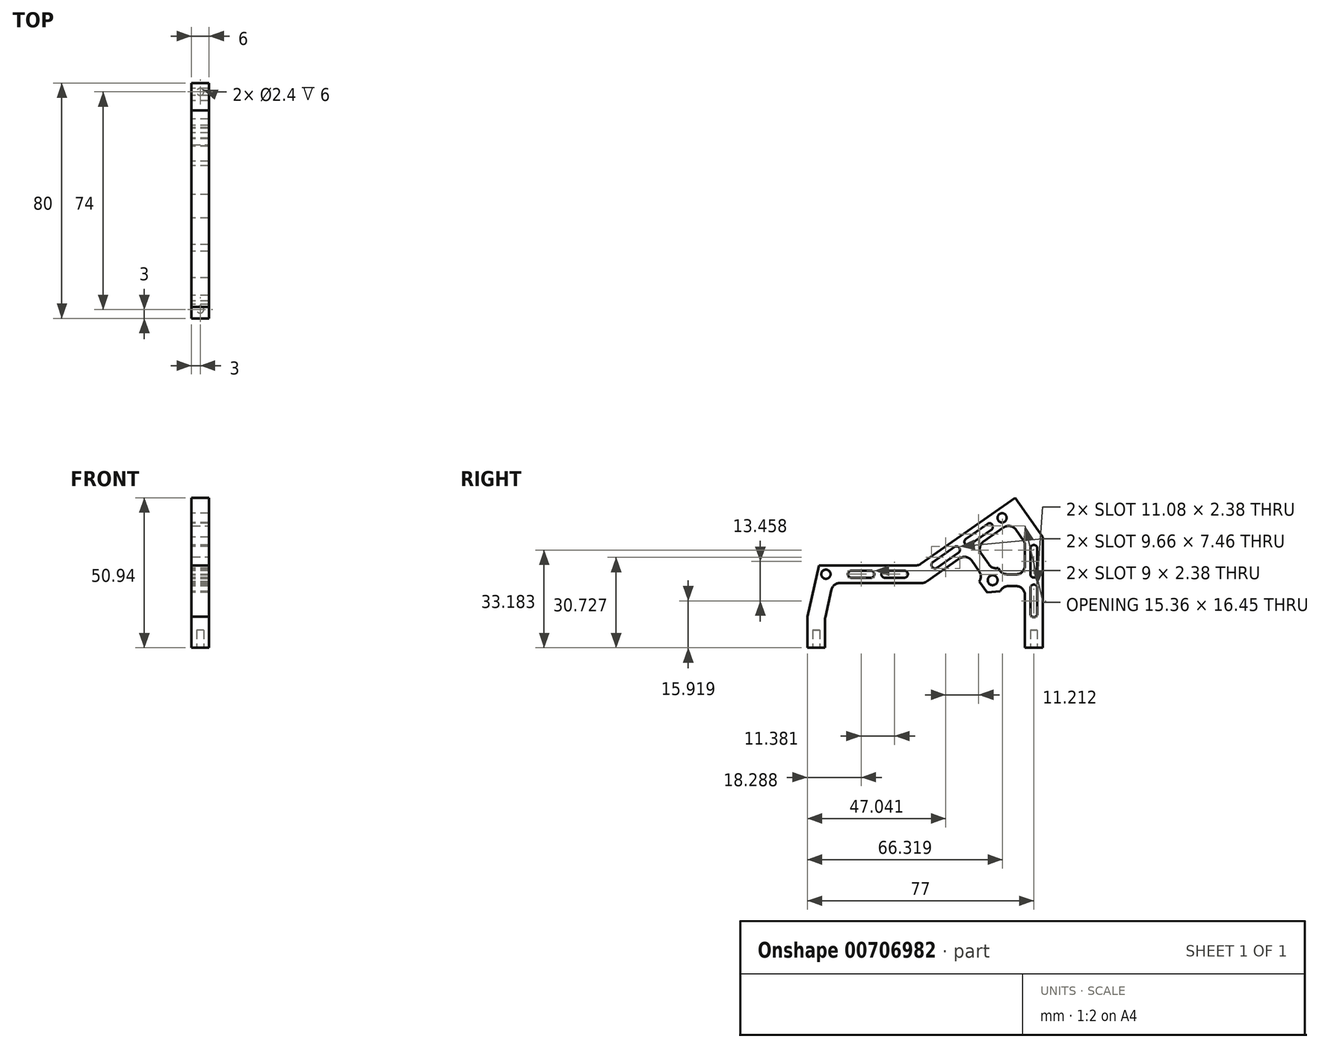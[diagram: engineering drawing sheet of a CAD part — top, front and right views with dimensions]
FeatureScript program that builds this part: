
annotation { "Feature Type Name" : "Feature", "Feature Type Description" : "" }
export const myFeature = defineFeature(function(context is Context, id is Id, definition is map)
    precondition{}
    {
        {
            var Q0;
            Q0=qCreatedBy(makeId("Top.planeOp"),FACE);
            var sketch = newSketch(context, id + "F0", { "sketchPlane" : qUnion([Q0])});
            skLineSegment(sketch, "E0", {"start": v(14, 40) * mm, "end": v(0, 40) * mm, "construction": true});
            skLineSegment(sketch, "E1", {"start": v(0, 40) * mm, "end": v(0, 0) * mm, "construction": true});
            skLineSegment(sketch, "E2", {"start": v(14, 40) * mm, "end": v(20, 40) * mm});
            skLineSegment(sketch, "E3", {"start": v(20, 40) * mm, "end": v(20, 0) * mm});
            skLineSegment(sketch, "E4", {"start": v(14, 40) * mm, "end": v(14, 0) * mm});
            skLineSegment(sketch, "E5.MirrorCS", {"start": v(14, -40) * mm, "end": v(20, -40) * mm});
            skLineSegment(sketch, "E6.MirrorCS", {"start": v(14, -40) * mm, "end": v(14, 0) * mm});
            skLineSegment(sketch, "E7.MirrorCS", {"start": v(20, -40) * mm, "end": v(20, 0) * mm});
            skLineSegment(sketch, "E8.MirrorCS", {"start": v(14, -40) * mm, "end": v(0, -40) * mm, "construction": true});
            skLineSegment(sketch, "E9.MirrorCS", {"start": v(0, -40) * mm, "end": v(0, 0) * mm, "construction": true});
            skLineSegment(sketch, "E10", {"start": v(14, 0) * mm, "end": v(29.88, 0) * mm, "construction": true});
            skLineSegment(sketch, "E11", {"start": v(20, 40) * mm, "end": v(20, 34) * mm, "construction": true});
            skPoint(sketch, "E12.centerSnap0", {"position": v(20, 37) * mm});
            skPoint(sketch, "E12.centerSnap1", {"position": v(17, 40) * mm});
            skSolve(sketch);
        }
        {
            var Q0;
            Q0=makeQuery(id+"F0.imprint","IMPRINT",FACE,{"disambiguationData":[TD([[makeQuery(id+"F0.imprint","IMPRINT",EDGE,{"derivedFrom":sQuery(id+"F0.wireOp",EDGE,"E2")}),-1.0]])]});
            extrude(context, id + "F1", {"entities" : qUnion([Q0]), "depth" : 70 * mm, "offsetDistance" : 25 * mm});
        }
        {
            var Q0;
            Q0=makeQuery(id+"F1.opExtrude","SWEPT_FACE",FACE,{"disambiguationData":[OSD([sQuery(id+"F0.wireOp",EDGE,"E4"),sQuery(id+"F0.wireOp",EDGE,"E6.MirrorCS")])]});
            var sketch = newSketch(context, id + "F2", { "sketchPlane" : qUnion([Q0])});
            skLineSegment(sketch, "E13", {"start": v(0, 0) * mm, "end": v(0, 28) * mm, "construction": true});
            skPoint(sketch, "E13.endSnap0", {"position": v(0, 0) * mm});
            skLineSegment(sketch, "E14", {"start": v(-20.33, 28) * mm, "end": v(19.67, 28) * mm, "construction": true});
            skLineSegment(sketch, "E15", {"start": v(2.08, 28) * mm, "end": v(-30.68, 50.94) * mm});
            skLineSegment(sketch, "E16", {"start": v(40, 10.6) * mm, "end": v(36.08, 28) * mm});
            skLineSegment(sketch, "E17", {"start": v(36.08, 28) * mm, "end": v(2.08, 28) * mm});
            skLineSegment(sketch, "E18", {"start": v(-30.68, 50.94) * mm, "end": v(-40, 37.64) * mm});
            skLineSegment(sketch, "E19", {"start": v(-40, 37.64) * mm, "end": v(-40, 0) * mm});
            skLineSegment(sketch, "E20", {"start": v(31.28, 22) * mm, "end": v(0.2, 22) * mm});
            skLineSegment(sketch, "E21", {"start": v(0.2, 22) * mm, "end": v(-14.18, 32.07) * mm});
            skLineSegment(sketch, "E22", {"start": v(-29.2, 42.59) * mm, "end": v(-34, 35.74) * mm});
            skLineSegment(sketch, "E23", {"start": v(-34, 35.74) * mm, "end": v(-34, 24.96) * mm});
            skLineSegment(sketch, "E24", {"start": v(-14.18, 32.07) * mm, "end": v(-21.96, 20.96) * mm});
            skLineSegment(sketch, "E25", {"start": v(-21.96, 20.96) * mm, "end": v(-34, 20.96) * mm});
            skLineSegment(sketch, "E26", {"start": v(-17.46, 34.36) * mm, "end": v(-24.04, 24.96) * mm});
            skLineSegment(sketch, "E27", {"start": v(-24.04, 24.96) * mm, "end": v(-34, 24.96) * mm});
            skLineSegment(sketch, "E28", {"start": v(-24.04, 24.96) * mm, "end": v(-21.96, 20.96) * mm, "construction": true});
            skCircle(sketch, "E29", {"center": v(-23, 22.96) * mm, "radius": 1.69 * mm});
            skLineSegment(sketch, "E30.trimOffspring", {"start": v(-17.46, 34.36) * mm, "end": v(-29.2, 42.59) * mm});
            skLineSegment(sketch, "E31.trimOffspring", {"start": v(-34, 20.96) * mm, "end": v(-34, 0) * mm});
            skLineSegment(sketch, "E32", {"start": v(-24.5, 46.6) * mm, "end": v(-26.21, 44.15) * mm, "construction": true});
            skCircle(sketch, "E33", {"center": v(-26.21, 44.15) * mm, "radius": 1.57 * mm});
            skLineSegment(sketch, "E34", {"start": v(36.08, 28) * mm, "end": v(31.28, 22) * mm, "construction": true});
            skCircle(sketch, "E35", {"center": v(33.68, 25) * mm, "radius": 1.57 * mm});
            skCircle(sketch, "E36.cCircle", {"center": v(-23, 22.96) * mm, "radius": 3.92 * mm, "construction": true});
            skLineSegment(sketch, "E36.0", {"start": v(-27.51, 23.35) * mm, "end": v(-24.92, 27.06) * mm});
            skLineSegment(sketch, "E36.1", {"start": v(-24.92, 27.06) * mm, "end": v(-20.4, 26.67) * mm});
            skLineSegment(sketch, "E36.2", {"start": v(-20.4, 26.67) * mm, "end": v(-18.5, 22.56) * mm});
            skLineSegment(sketch, "E36.3", {"start": v(-18.5, 22.56) * mm, "end": v(-21.09, 18.85) * mm});
            skLineSegment(sketch, "E36.4", {"start": v(-21.09, 18.85) * mm, "end": v(-25.6, 19.25) * mm});
            skLineSegment(sketch, "E36.5", {"start": v(-25.6, 19.25) * mm, "end": v(-27.51, 23.35) * mm});
            skPoint(sketch, "E36.0.midPoint", {"position": v(-26.21, 25.2) * mm});
            skLineSegment(sketch, "E37", {"start": v(-30.68, 50.94) * mm, "end": v(-30.68, 0) * mm, "construction": true});
            skLineSegment(sketch, "E38", {"start": v(-49.75, 0) * mm, "end": v(34, 0) * mm, "construction": true});
            skLineSegment(sketch, "E39", {"start": v(40, 10.6) * mm, "end": v(40, 0) * mm});
            skLineSegment(sketch, "E40", {"start": v(40, 0) * mm, "end": v(36.1, 0) * mm});
            skLineSegment(sketch, "E41", {"start": v(34, 9.92) * mm, "end": v(34, 0) * mm});
            skLineSegment(sketch, "E42.trimOffspring", {"start": v(42.25, 0) * mm, "end": v(49.74, 0) * mm, "construction": true});
            skLineSegment(sketch, "E43", {"start": v(40, 0) * mm, "end": v(34, 0) * mm});
            skLineSegment(sketch, "E44", {"start": v(31.28, 22) * mm, "end": v(34, 9.92) * mm});
            skLineSegment(sketch, "E45", {"start": v(0.2, 22) * mm, "end": v(31.28, 22) * mm});
            skLineSegment(sketch, "E46", {"start": v(40, 0) * mm, "end": v(40, 10.6) * mm});
            skLineSegment(sketch, "E47", {"start": v(7.02, 26.2) * mm, "end": v(13.64, 26.2) * mm});
            skLineSegment(sketch, "E48", {"start": v(2.08, 28) * mm, "end": v(2.08, 22) * mm, "construction": true});
            skLineSegment(sketch, "E49", {"start": v(7.02, 23.8) * mm, "end": v(7.02, 26.2) * mm, "construction": true});
            skLineSegment(sketch, "E50", {"start": v(25.02, 23.8) * mm, "end": v(25.02, 26.2) * mm, "construction": true});
            skCircle(sketch, "E51", {"center": v(7.02, 25) * mm, "radius": 1.2 * mm});
            skCircle(sketch, "E52", {"center": v(25.02, 25) * mm, "radius": 1.2 * mm});
            skLineSegment(sketch, "E53", {"start": v(-35.8, 33.72) * mm, "end": v(-35.8, 25.03) * mm});
            skLineSegment(sketch, "E54", {"start": v(-38.2, 33.72) * mm, "end": v(-38.2, 25.03) * mm});
            skLineSegment(sketch, "E55", {"start": v(-35.8, 33.72) * mm, "end": v(-38.2, 33.72) * mm, "construction": true});
            skLineSegment(sketch, "E56", {"start": v(-35.8, 11.57) * mm, "end": v(-38.2, 11.57) * mm, "construction": true});
            skCircle(sketch, "E57", {"center": v(-37, 33.72) * mm, "radius": 1.2 * mm});
            skCircle(sketch, "E58", {"center": v(-37, 11.57) * mm, "radius": 1.2 * mm});
            skLineSegment(sketch, "E59", {"start": v(-22.6, 40.16) * mm, "end": v(-15.28, 35.04) * mm});
            skLineSegment(sketch, "E60", {"start": v(-22.6, 40.16) * mm, "end": v(-21.23, 42.11) * mm, "construction": true});
            skLineSegment(sketch, "E61", {"start": v(-21.23, 42.11) * mm, "end": v(-13.92, 37) * mm});
            skLineSegment(sketch, "E62", {"start": v(-2.7, 29.14) * mm, "end": v(-4.07, 27.2) * mm, "construction": true});
            skCircle(sketch, "E63", {"center": v(-21.9, 41.14) * mm, "radius": 1.2 * mm});
            skCircle(sketch, "E64", {"center": v(-3.39, 28.17) * mm, "radius": 1.2 * mm});
            skLineSegment(sketch, "E65", {"start": v(5.46, 28) * mm, "end": v(5.46, 22) * mm, "construction": true});
            skLineSegment(sketch, "E66", {"start": v(5.46, 25) * mm, "end": v(7.02, 25) * mm, "construction": true});
            skLineSegment(sketch, "E67", {"start": v(-22.05, 44.9) * mm, "end": v(-25.5, 39.98) * mm, "construction": true});
            skLineSegment(sketch, "E68", {"start": v(-23.77, 42.44) * mm, "end": v(-21.9, 41.14) * mm, "construction": true});
            skLineSegment(sketch, "E69", {"start": v(-34, 35.47) * mm, "end": v(-40, 35.47) * mm, "construction": true});
            skLineSegment(sketch, "E70", {"start": v(-37, 35.47) * mm, "end": v(-37, 33.72) * mm, "construction": true});
            skLineSegment(sketch, "E71", {"start": v(16.02, 26.2) * mm, "end": v(16.02, 23.8) * mm, "construction": true});
            skLineSegment(sketch, "E72", {"start": v(-35.8, 22.65) * mm, "end": v(-38.2, 22.65) * mm, "construction": true});
            skLineSegment(sketch, "E73", {"start": v(-12.65, 34.65) * mm, "end": v(-21.9, 41.14) * mm, "construction": true});
            skLineSegment(sketch, "E74", {"start": v(-12.65, 34.65) * mm, "end": v(-3.39, 28.17) * mm, "construction": true});
            skLineSegment(sketch, "E75", {"start": v(25.02, 25) * mm, "end": v(7.02, 25) * mm, "construction": true});
            skCircle(sketch, "E76", {"center": v(13.64, 25) * mm, "radius": 1.2 * mm});
            skCircle(sketch, "E77", {"center": v(18.4, 25) * mm, "radius": 1.2 * mm});
            skCircle(sketch, "E78", {"center": v(-10.7, 33.29) * mm, "radius": 1.2 * mm});
            skCircle(sketch, "E79", {"center": v(-14.6, 36.02) * mm, "radius": 1.2 * mm});
            skLineSegment(sketch, "E80", {"start": v(-37, 33.72) * mm, "end": v(-37, 11.57) * mm, "construction": true});
            skCircle(sketch, "E81", {"center": v(-37, 25.03) * mm, "radius": 1.2 * mm});
            skCircle(sketch, "E82", {"center": v(-37, 20.27) * mm, "radius": 1.2 * mm});
            skLineSegment(sketch, "E83.trimOffspring", {"start": v(-11.38, 32.31) * mm, "end": v(-4.07, 27.2) * mm});
            skPoint(sketch, "E84.orphan", {"position": v(-13.33, 33.68) * mm});
            skPoint(sketch, "E85.start.orphan", {"position": v(-11.96, 35.63) * mm});
            skLineSegment(sketch, "E86.trimOffspring", {"start": v(-10.01, 34.26) * mm, "end": v(-2.7, 29.14) * mm});
            skLineSegment(sketch, "E87.trimOffspring", {"start": v(18.4, 23.8) * mm, "end": v(25.02, 23.8) * mm});
            skLineSegment(sketch, "E88.trimOffspring", {"start": v(18.4, 26.2) * mm, "end": v(25.02, 26.2) * mm});
            skLineSegment(sketch, "E89", {"start": v(7.02, 23.8) * mm, "end": v(13.64, 23.8) * mm});
            skLineSegment(sketch, "E90.trimOffspring", {"start": v(-35.8, 20.27) * mm, "end": v(-35.8, 11.57) * mm});
            skLineSegment(sketch, "E91.trimOffspring", {"start": v(-38.2, 20.27) * mm, "end": v(-38.2, 11.57) * mm});
            skSolve(sketch);
        }
        {
            var Q0;
            {var subQ1=sQuery(id+"F2.wireOp",EDGE,"E21");Q0=makeQuery(id+"F2.imprint","IMPRINT",FACE,{"disambiguationData":[TD([[makeQuery(id+"F2.imprint","IMPRINT",EDGE,{"derivedFrom":subQ1}),1.0]])]});}
            var Q1;
            Q1=makeQuery(id+"F2.imprint","IMPRINT",FACE,{"disambiguationData":[TD([[makeQuery(id+"F2.imprint","IMPRINT",EDGE,{"derivedFrom":sQuery(id+"F2.wireOp",EDGE,"E22")}),1.0]])]});
            var Q2;
            Q2=makeQuery(id+"F2.imprint","IMPRINT",FACE,{"disambiguationData":[TD([[makeQuery(id+"F2.imprint","IMPRINT",EDGE,{"derivedFrom":sQuery(id+"F2.wireOp",EDGE,"E15")}),-1.0]])]});
            var Q3;
            Q3=makeQuery(id+"F2.imprint","IMPRINT",FACE,{"disambiguationData":[TD([[makeQuery(id+"F2.imprint","IMPRINT",EDGE,{"derivedFrom":sQuery(id+"F2.wireOp",EDGE,"E33")}),1.0]])]});
            var Q4;
            Q4=makeQuery(id+"F2.imprint","IMPRINT",FACE,{"disambiguationData":[TD([[makeQuery(id+"F2.imprint","IMPRINT",EDGE,{"derivedFrom":sQuery(id+"F2.wireOp",EDGE,"E29")}),1.0]])]});
            var Q5;
            Q5=makeQuery(id+"F2.imprint","IMPRINT",FACE,{"disambiguationData":[TD([[makeQuery(id+"F2.imprint","IMPRINT",EDGE,{"derivedFrom":sQuery(id+"F2.wireOp",EDGE,"E35")}),1.0]])]});
            var Q6;
            {var subQ0=sQuery(id+"F2.wireOp",EDGE,"E51");var subQ1=makeQuery(id+"F2.imprint","INTERSECT",VERTEX,{"derivedFrom":[sQuery(id+"F2.wireOp",EDGE,"E47"),subQ0]});Q6=makeQuery(id+"F2.imprint","IMPRINT",FACE,{"disambiguationData":[TD([[makeQuery(id+"F2.imprint","IMPRINT",EDGE,{"disambiguationData":[TD([[subQ1,-1.0]])],"derivedFrom":subQ0}),1.0]])]});}
            var Q7;
            {var subQ0=sQuery(id+"F2.wireOp",EDGE,"E52");var subQ1=makeQuery(id+"F2.imprint","INTERSECT",VERTEX,{"derivedFrom":[sQuery(id+"F2.wireOp",EDGE,"E47"),subQ0]});Q7=makeQuery(id+"F2.imprint","IMPRINT",FACE,{"disambiguationData":[TD([[makeQuery(id+"F2.imprint","IMPRINT",EDGE,{"disambiguationData":[TD([[subQ1,-1.0]])],"derivedFrom":subQ0}),1.0]])]});}
            var Q8;
            {var subQ0=sQuery(id+"F2.wireOp",EDGE,"E57");var subQ1=makeQuery(id+"F2.imprint","INTERSECT",VERTEX,{"derivedFrom":[sQuery(id+"F2.wireOp",EDGE,"E53"),subQ0]});Q8=makeQuery(id+"F2.imprint","IMPRINT",FACE,{"disambiguationData":[TD([[makeQuery(id+"F2.imprint","IMPRINT",EDGE,{"disambiguationData":[TD([[subQ1,-1.0]])],"derivedFrom":subQ0}),1.0]])]});}
            var Q9;
            {var subQ0=sQuery(id+"F2.wireOp",EDGE,"E58");var subQ1=makeQuery(id+"F2.imprint","INTERSECT",VERTEX,{"derivedFrom":[sQuery(id+"F2.wireOp",EDGE,"E53"),subQ0]});Q9=makeQuery(id+"F2.imprint","IMPRINT",FACE,{"disambiguationData":[TD([[makeQuery(id+"F2.imprint","IMPRINT",EDGE,{"disambiguationData":[TD([[subQ1,-1.0]])],"derivedFrom":subQ0}),1.0]])]});}
            var Q10;
            {var subQ0=sQuery(id+"F2.wireOp",EDGE,"E63");var subQ1=makeQuery(id+"F2.imprint","INTERSECT",VERTEX,{"derivedFrom":[sQuery(id+"F2.wireOp",EDGE,"E59"),subQ0]});Q10=makeQuery(id+"F2.imprint","IMPRINT",FACE,{"disambiguationData":[TD([[makeQuery(id+"F2.imprint","IMPRINT",EDGE,{"disambiguationData":[TD([[subQ1,1.0]])],"derivedFrom":subQ0}),1.0]])]});}
            var Q11;
            {var subQ0=sQuery(id+"F2.wireOp",EDGE,"E64");var subQ1=makeQuery(id+"F2.imprint","INTERSECT",VERTEX,{"derivedFrom":[sQuery(id+"F2.wireOp",EDGE,"E59"),subQ0]});Q11=makeQuery(id+"F2.imprint","IMPRINT",FACE,{"disambiguationData":[TD([[makeQuery(id+"F2.imprint","IMPRINT",EDGE,{"disambiguationData":[TD([[subQ1,1.0]])],"derivedFrom":subQ0}),1.0]])]});}
            var Q12;
            {var subQ0=sQuery(id+"F2.wireOp",EDGE,"E58");var subQ1=sQuery(id+"F2.wireOp",EDGE,"E53");var subQ2=makeQuery(id+"F2.imprint","INTERSECT",VERTEX,{"derivedFrom":[subQ1,subQ0]});Q12=makeQuery(id+"F2.imprint","IMPRINT",FACE,{"disambiguationData":[TD([[makeQuery(id+"F2.imprint","IMPRINT",EDGE,{"disambiguationData":[TD([[subQ2,1.0]])],"derivedFrom":subQ1}),-1.0]])]});}
            var Q13;
            {var subQ0=sQuery(id+"F2.wireOp",EDGE,"E82");var subQ1=sQuery(id+"F2.wireOp",EDGE,"EsRLWaQp-72Lr-nXQH-179a-LBt1Ee8kWsKf");var subQ2=makeQuery(id+"F2.imprint","INTERSECT",VERTEX,{"disambiguationData":[OD(0.0)],"derivedFrom":[subQ1,subQ0]});Q13=makeQuery(id+"F2.imprint","IMPRINT",FACE,{"disambiguationData":[TD([[makeQuery(id+"F2.imprint","IMPRINT",EDGE,{"disambiguationData":[TD([[subQ2,-1.0]])],"derivedFrom":subQ1}),-1.0]])]});}
            var Q14;
            {var subQ0=sQuery(id+"F2.wireOp",EDGE,"E82");var subQ1=sQuery(id+"F2.wireOp",EDGE,"EsRLWaQp-72Lr-nXQH-179a-LBt1Ee8kWsKf");var subQ2=makeQuery(id+"F2.imprint","INTERSECT",VERTEX,{"disambiguationData":[OD(0.0)],"derivedFrom":[subQ1,subQ0]});Q14=makeQuery(id+"F2.imprint","IMPRINT",FACE,{"disambiguationData":[TD([[makeQuery(id+"F2.imprint","IMPRINT",EDGE,{"disambiguationData":[TD([[subQ2,-1.0]])],"derivedFrom":subQ1}),1.0]])]});}
            var Q15;
            {var subQ0=sQuery(id+"F2.wireOp",EDGE,"E57");var subQ1=sQuery(id+"F2.wireOp",EDGE,"E53");var subQ2=makeQuery(id+"F2.imprint","INTERSECT",VERTEX,{"derivedFrom":[subQ1,subQ0]});Q15=makeQuery(id+"F2.imprint","IMPRINT",FACE,{"disambiguationData":[TD([[makeQuery(id+"F2.imprint","IMPRINT",EDGE,{"disambiguationData":[TD([[subQ2,-1.0]])],"derivedFrom":subQ1}),-1.0]])]});}
            var Q16;
            {var subQ0=sQuery(id+"F2.wireOp",EDGE,"E81");var subQ1=sQuery(id+"F2.wireOp",EDGE,"dPTXOL7o-P8y6-gZZ0-hFhJ-cb4R31KIsnZc");var subQ2=makeQuery(id+"F2.imprint","INTERSECT",VERTEX,{"disambiguationData":[OD(0.0)],"derivedFrom":[subQ1,subQ0]});Q16=makeQuery(id+"F2.imprint","IMPRINT",FACE,{"disambiguationData":[TD([[makeQuery(id+"F2.imprint","IMPRINT",EDGE,{"disambiguationData":[TD([[subQ2,-1.0]])],"derivedFrom":subQ1}),-1.0]])]});}
            var Q17;
            {var subQ0=sQuery(id+"F2.wireOp",EDGE,"E81");var subQ1=sQuery(id+"F2.wireOp",EDGE,"dPTXOL7o-P8y6-gZZ0-hFhJ-cb4R31KIsnZc");var subQ2=makeQuery(id+"F2.imprint","INTERSECT",VERTEX,{"disambiguationData":[OD(0.0)],"derivedFrom":[subQ1,subQ0]});Q17=makeQuery(id+"F2.imprint","IMPRINT",FACE,{"disambiguationData":[TD([[makeQuery(id+"F2.imprint","IMPRINT",EDGE,{"disambiguationData":[TD([[subQ2,-1.0]])],"derivedFrom":subQ1}),1.0]])]});}
            var Q18;
            {var subQ0=sQuery(id+"F2.wireOp",EDGE,"E63");var subQ1=sQuery(id+"F2.wireOp",EDGE,"E59");var subQ2=makeQuery(id+"F2.imprint","INTERSECT",VERTEX,{"derivedFrom":[subQ1,subQ0]});Q18=makeQuery(id+"F2.imprint","IMPRINT",FACE,{"disambiguationData":[TD([[makeQuery(id+"F2.imprint","IMPRINT",EDGE,{"disambiguationData":[TD([[subQ2,-1.0]])],"derivedFrom":subQ1}),1.0]])]});}
            var Q19;
            {var subQ0=sQuery(id+"F2.wireOp",EDGE,"E79");var subQ1=sQuery(id+"F2.wireOp",EDGE,"iujlU8PM-xRd4-Xfqd-nS0c-G3hk0IdFOhpx");var subQ2=makeQuery(id+"F2.imprint","INTERSECT",VERTEX,{"disambiguationData":[OD(0.0)],"derivedFrom":[subQ1,subQ0]});Q19=makeQuery(id+"F2.imprint","IMPRINT",FACE,{"disambiguationData":[TD([[makeQuery(id+"F2.imprint","IMPRINT",EDGE,{"disambiguationData":[TD([[subQ2,-1.0]])],"derivedFrom":subQ1}),-1.0]])]});}
            var Q20;
            {var subQ0=sQuery(id+"F2.wireOp",EDGE,"E79");var subQ1=sQuery(id+"F2.wireOp",EDGE,"iujlU8PM-xRd4-Xfqd-nS0c-G3hk0IdFOhpx");var subQ2=makeQuery(id+"F2.imprint","INTERSECT",VERTEX,{"disambiguationData":[OD(0.0)],"derivedFrom":[subQ1,subQ0]});Q20=makeQuery(id+"F2.imprint","IMPRINT",FACE,{"disambiguationData":[TD([[makeQuery(id+"F2.imprint","IMPRINT",EDGE,{"disambiguationData":[TD([[subQ2,-1.0]])],"derivedFrom":subQ1}),1.0]])]});}
            var Q21;
            {var subQ0=sQuery(id+"F2.wireOp",EDGE,"E64");var subQ1=sQuery(id+"F2.wireOp",EDGE,"E59");var subQ2=makeQuery(id+"F2.imprint","INTERSECT",VERTEX,{"derivedFrom":[subQ1,subQ0]});Q21=makeQuery(id+"F2.imprint","IMPRINT",FACE,{"disambiguationData":[TD([[makeQuery(id+"F2.imprint","IMPRINT",EDGE,{"disambiguationData":[TD([[subQ2,1.0]])],"derivedFrom":subQ1}),1.0]])]});}
            var Q22;
            {var subQ0=sQuery(id+"F2.wireOp",EDGE,"E78");var subQ1=sQuery(id+"F2.wireOp",EDGE,"WhBVlu8J-ggpT-rPkh-PH5j-TZSZnhHrwUjz");var subQ2=makeQuery(id+"F2.imprint","INTERSECT",VERTEX,{"disambiguationData":[OD(0.0)],"derivedFrom":[subQ1,subQ0]});Q22=makeQuery(id+"F2.imprint","IMPRINT",FACE,{"disambiguationData":[TD([[makeQuery(id+"F2.imprint","IMPRINT",EDGE,{"disambiguationData":[TD([[subQ2,1.0]])],"derivedFrom":subQ1}),-1.0]])]});}
            var Q23;
            {var subQ0=sQuery(id+"F2.wireOp",EDGE,"E78");var subQ1=sQuery(id+"F2.wireOp",EDGE,"WhBVlu8J-ggpT-rPkh-PH5j-TZSZnhHrwUjz");var subQ2=makeQuery(id+"F2.imprint","INTERSECT",VERTEX,{"disambiguationData":[OD(0.0)],"derivedFrom":[subQ1,subQ0]});Q23=makeQuery(id+"F2.imprint","IMPRINT",FACE,{"disambiguationData":[TD([[makeQuery(id+"F2.imprint","IMPRINT",EDGE,{"disambiguationData":[TD([[subQ2,1.0]])],"derivedFrom":subQ1}),1.0]])]});}
            var Q24;
            {var subQ0=sQuery(id+"F2.wireOp",EDGE,"E51");var subQ1=sQuery(id+"F2.wireOp",EDGE,"E47");var subQ2=makeQuery(id+"F2.imprint","INTERSECT",VERTEX,{"derivedFrom":[subQ1,subQ0]});Q24=makeQuery(id+"F2.imprint","IMPRINT",FACE,{"disambiguationData":[TD([[makeQuery(id+"F2.imprint","IMPRINT",EDGE,{"disambiguationData":[TD([[subQ2,-1.0]])],"derivedFrom":subQ1}),-1.0]])]});}
            var Q25;
            {var subQ0=sQuery(id+"F2.wireOp",EDGE,"E76");var subQ1=sQuery(id+"F2.wireOp",EDGE,"A0GBhmAl-cezT-vBN6-2keo-XJEfcKbMd6cT");var subQ2=makeQuery(id+"F2.imprint","INTERSECT",VERTEX,{"disambiguationData":[OD(0.0)],"derivedFrom":[subQ1,subQ0]});Q25=makeQuery(id+"F2.imprint","IMPRINT",FACE,{"disambiguationData":[TD([[makeQuery(id+"F2.imprint","IMPRINT",EDGE,{"disambiguationData":[TD([[subQ2,-1.0]])],"derivedFrom":subQ1}),-1.0]])]});}
            var Q26;
            {var subQ0=sQuery(id+"F2.wireOp",EDGE,"E76");var subQ1=sQuery(id+"F2.wireOp",EDGE,"A0GBhmAl-cezT-vBN6-2keo-XJEfcKbMd6cT");var subQ2=makeQuery(id+"F2.imprint","INTERSECT",VERTEX,{"disambiguationData":[OD(0.0)],"derivedFrom":[subQ1,subQ0]});Q26=makeQuery(id+"F2.imprint","IMPRINT",FACE,{"disambiguationData":[TD([[makeQuery(id+"F2.imprint","IMPRINT",EDGE,{"disambiguationData":[TD([[subQ2,-1.0]])],"derivedFrom":subQ1}),1.0]])]});}
            var Q27;
            {var subQ0=sQuery(id+"F2.wireOp",EDGE,"E52");var subQ1=sQuery(id+"F2.wireOp",EDGE,"E47");var subQ2=makeQuery(id+"F2.imprint","INTERSECT",VERTEX,{"derivedFrom":[subQ1,subQ0]});Q27=makeQuery(id+"F2.imprint","IMPRINT",FACE,{"disambiguationData":[TD([[makeQuery(id+"F2.imprint","IMPRINT",EDGE,{"disambiguationData":[TD([[subQ2,1.0]])],"derivedFrom":subQ1}),-1.0]])]});}
            var Q28;
            {var subQ0=sQuery(id+"F2.wireOp",EDGE,"E77");var subQ1=sQuery(id+"F2.wireOp",EDGE,"UBjIhsa9-i5sD-a0D1-aE2p-8xy051tw6F00");var subQ2=makeQuery(id+"F2.imprint","INTERSECT",VERTEX,{"disambiguationData":[OD(0.0)],"derivedFrom":[subQ1,subQ0]});Q28=makeQuery(id+"F2.imprint","IMPRINT",FACE,{"disambiguationData":[TD([[makeQuery(id+"F2.imprint","IMPRINT",EDGE,{"disambiguationData":[TD([[subQ2,1.0]])],"derivedFrom":subQ1}),-1.0]])]});}
            var Q29;
            {var subQ0=sQuery(id+"F2.wireOp",EDGE,"E77");var subQ1=sQuery(id+"F2.wireOp",EDGE,"UBjIhsa9-i5sD-a0D1-aE2p-8xy051tw6F00");var subQ2=makeQuery(id+"F2.imprint","INTERSECT",VERTEX,{"disambiguationData":[OD(0.0)],"derivedFrom":[subQ1,subQ0]});Q29=makeQuery(id+"F2.imprint","IMPRINT",FACE,{"disambiguationData":[TD([[makeQuery(id+"F2.imprint","IMPRINT",EDGE,{"disambiguationData":[TD([[subQ2,1.0]])],"derivedFrom":subQ1}),1.0]])]});}
            var Q30;
            {var subQ0=sQuery(id+"F2.wireOp",EDGE,"E90.trimOffspring");Q30=makeQuery(id+"F2.imprint","IMPRINT",FACE,{"disambiguationData":[TD([[makeQuery(id+"F2.imprint","IMPRINT",EDGE,{"derivedFrom":subQ0}),-1.0]])]});}
            var Q31;
            {var subQ0=sQuery(id+"F2.wireOp",EDGE,"E82");var subQ1=makeQuery(id+"F2.imprint","INTERSECT",VERTEX,{"derivedFrom":[subQ0,sQuery(id+"F2.wireOp",EDGE,"E90.trimOffspring")]});Q31=makeQuery(id+"F2.imprint","IMPRINT",FACE,{"disambiguationData":[TD([[makeQuery(id+"F2.imprint","IMPRINT",EDGE,{"disambiguationData":[TD([[subQ1,-1.0]])],"derivedFrom":subQ0}),1.0]])]});}
            var Q32;
            {var subQ0=sQuery(id+"F2.wireOp",EDGE,"E81");var subQ1=makeQuery(id+"F2.imprint","INTERSECT",VERTEX,{"derivedFrom":[sQuery(id+"F2.wireOp",EDGE,"E53"),subQ0]});Q32=makeQuery(id+"F2.imprint","IMPRINT",FACE,{"disambiguationData":[TD([[makeQuery(id+"F2.imprint","IMPRINT",EDGE,{"disambiguationData":[TD([[subQ1,-1.0]])],"derivedFrom":subQ0}),1.0]])]});}
            var Q33;
            {var subQ0=sQuery(id+"F2.wireOp",EDGE,"E79");var subQ1=makeQuery(id+"F2.imprint","INTERSECT",VERTEX,{"derivedFrom":[sQuery(id+"F2.wireOp",EDGE,"E59"),subQ0]});Q33=makeQuery(id+"F2.imprint","IMPRINT",FACE,{"disambiguationData":[TD([[makeQuery(id+"F2.imprint","IMPRINT",EDGE,{"disambiguationData":[TD([[subQ1,1.0]])],"derivedFrom":subQ0}),1.0]])]});}
            var Q34;
            {var subQ0=sQuery(id+"F2.wireOp",EDGE,"E78");var subQ1=makeQuery(id+"F2.imprint","INTERSECT",VERTEX,{"derivedFrom":[subQ0,sQuery(id+"F2.wireOp",EDGE,"E83.trimOffspring")]});Q34=makeQuery(id+"F2.imprint","IMPRINT",FACE,{"disambiguationData":[TD([[makeQuery(id+"F2.imprint","IMPRINT",EDGE,{"disambiguationData":[TD([[subQ1,1.0]])],"derivedFrom":subQ0}),1.0]])]});}
            var Q35;
            {var subQ0=sQuery(id+"F2.wireOp",EDGE,"E83.trimOffspring");Q35=makeQuery(id+"F2.imprint","IMPRINT",FACE,{"disambiguationData":[TD([[makeQuery(id+"F2.imprint","IMPRINT",EDGE,{"derivedFrom":subQ0}),1.0]])]});}
            var Q36;
            {var subQ0=sQuery(id+"F2.wireOp",EDGE,"E76");var subQ1=makeQuery(id+"F2.imprint","INTERSECT",VERTEX,{"derivedFrom":[sQuery(id+"F2.wireOp",EDGE,"E47"),subQ0]});Q36=makeQuery(id+"F2.imprint","IMPRINT",FACE,{"disambiguationData":[TD([[makeQuery(id+"F2.imprint","IMPRINT",EDGE,{"disambiguationData":[TD([[subQ1,-1.0]])],"derivedFrom":subQ0}),1.0]])]});}
            var Q37;
            {var subQ0=sQuery(id+"F2.wireOp",EDGE,"E77");var subQ1=makeQuery(id+"F2.imprint","INTERSECT",VERTEX,{"derivedFrom":[subQ0,sQuery(id+"F2.wireOp",EDGE,"E87.trimOffspring")]});Q37=makeQuery(id+"F2.imprint","IMPRINT",FACE,{"disambiguationData":[TD([[makeQuery(id+"F2.imprint","IMPRINT",EDGE,{"disambiguationData":[TD([[subQ1,1.0]])],"derivedFrom":subQ0}),1.0]])]});}
            var Q38;
            {var subQ0=sQuery(id+"F2.wireOp",EDGE,"E87.trimOffspring");Q38=makeQuery(id+"F2.imprint","IMPRINT",FACE,{"disambiguationData":[TD([[makeQuery(id+"F2.imprint","IMPRINT",EDGE,{"derivedFrom":subQ0}),1.0]])]});}
            extrude(context, id + "F3", {"entities" : qUnion([Q0, Q1, Q2, Q3, Q4, Q5, Q6, Q7, Q8, Q9, Q10, Q11, Q12, Q13, Q14, Q15, Q16, Q17, Q18, Q19, Q20, Q21, Q22, Q23, Q24, Q25, Q26, Q27, Q28, Q29, Q30, Q31, Q32, Q33, Q34, Q35, Q36, Q37, Q38]), "operationType" : NewBodyOperationType.REMOVE, "oppositeDirection" : true, "depth" : 25 * mm, "offsetDistance" : 25 * mm});
        }
        {
            var Q0;
            Q0=makeQuery(id+"F0.imprint","IMPRINT",FACE,{"disambiguationData":[TD([[makeQuery(id+"F0.imprint","IMPRINT",EDGE,{"derivedFrom":sQuery(id+"F0.wireOp",EDGE,"E2")}),-1.0]])]});
            var sketch = newSketch(context, id + "F4", { "sketchPlane" : qUnion([Q0])});
            skLineSegment(sketch, "E92", {"start": v(0, 0) * mm, "end": v(0, 40) * mm, "construction": true});
            skLineSegment(sketch, "E93", {"start": v(0, 40) * mm, "end": v(14, 40) * mm, "construction": true});
            skLineSegment(sketch, "E94", {"start": v(14, 40) * mm, "end": v(20, 40) * mm, "construction": true});
            skLineSegment(sketch, "E95", {"start": v(20, 40) * mm, "end": v(20, 34) * mm, "construction": true});
            skLineSegment(sketch, "E96", {"start": v(20, 34) * mm, "end": v(14, 34) * mm, "construction": true});
            skLineSegment(sketch, "E97", {"start": v(14, 34) * mm, "end": v(14, 40) * mm, "construction": true});
            skCircle(sketch, "E98", {"center": v(17, 37) * mm, "radius": 1.2 * mm});
            skPoint(sketch, "E98.centerSnap0", {"position": v(20, 37) * mm});
            skPoint(sketch, "E98.centerSnap1", {"position": v(17, 34) * mm});
            skLineSegment(sketch, "E99", {"start": v(0, 0) * mm, "end": v(0, -40) * mm, "construction": true});
            skLineSegment(sketch, "E100", {"start": v(0, -40) * mm, "end": v(14, -40) * mm, "construction": true});
            skLineSegment(sketch, "E101", {"start": v(14, -40) * mm, "end": v(20, -40) * mm, "construction": true});
            skLineSegment(sketch, "E102", {"start": v(20, -40) * mm, "end": v(20, -34) * mm, "construction": true});
            skLineSegment(sketch, "E103", {"start": v(20, -34) * mm, "end": v(14, -34) * mm, "construction": true});
            skLineSegment(sketch, "E104", {"start": v(14, -34) * mm, "end": v(14, -40) * mm, "construction": true});
            skCircle(sketch, "E105", {"center": v(17, -37) * mm, "radius": 1.2 * mm});
            skPoint(sketch, "E105.centerSnap0", {"position": v(17, -40) * mm});
            skPoint(sketch, "E105.centerSnap1", {"position": v(20, -37) * mm});
            skSolve(sketch);
        }
        {
            var Q0;
            Q0=qSketchRegion(id+"F4",true);
            extrude(context, id + "F5", {"entities" : qUnion([Q0]), "operationType" : NewBodyOperationType.REMOVE, "depth" : 6 * mm, "offsetDistance" : 25 * mm});
        }
        {
            var Q0;
            Q0=makeQuery(id+"F3.boolean.opBoolean","COPY",EDGE,{"derivedFrom":makeQuery(id+"F3.opExtrude","SWEPT_EDGE",EDGE,{"disambiguationData":[OSD([sQuery(id+"F2.wireOp",EDGE,"E26"),sQuery(id+"F2.wireOp",EDGE,"E36.1")])]})});
            var Q1;
            Q1=makeQuery(id+"F3.boolean.opBoolean","COPY",EDGE,{"derivedFrom":makeQuery(id+"F3.opExtrude","SWEPT_EDGE",EDGE,{"disambiguationData":[OSD([sQuery(id+"F2.wireOp",EDGE,"E27"),sQuery(id+"F2.wireOp",EDGE,"E36.0")])]})});
            var Q2;
            Q2=makeQuery(id+"F3.boolean.opBoolean","COPY",EDGE,{"derivedFrom":makeQuery(id+"F3.opExtrude","SWEPT_EDGE",EDGE,{"disambiguationData":[OSD([sQuery(id+"F2.wireOp",EDGE,"E23"),sQuery(id+"F2.wireOp",EDGE,"E27")])]})});
            var Q3;
            Q3=makeQuery(id+"F3.boolean.opBoolean","COPY",EDGE,{"derivedFrom":makeQuery(id+"F3.opExtrude","SWEPT_EDGE",EDGE,{"disambiguationData":[OSD([sQuery(id+"F2.wireOp",EDGE,"E22"),sQuery(id+"F2.wireOp",EDGE,"E23")])]})});
            var Q4;
            Q4=makeQuery(id+"F3.boolean.opBoolean","COPY",EDGE,{"derivedFrom":makeQuery(id+"F3.opExtrude","SWEPT_EDGE",EDGE,{"disambiguationData":[OSD([sQuery(id+"F2.wireOp",EDGE,"E22"),sQuery(id+"F2.wireOp",EDGE,"E30.trimOffspring")])]})});
            var Q5;
            Q5=makeQuery(id+"F3.boolean.opBoolean","COPY",EDGE,{"derivedFrom":makeQuery(id+"F3.opExtrude","SWEPT_EDGE",EDGE,{"disambiguationData":[OSD([sQuery(id+"F2.wireOp",EDGE,"E26"),sQuery(id+"F2.wireOp",EDGE,"E30.trimOffspring")])]})});
            var Q6;
            Q6=makeQuery(id+"F3.boolean.opBoolean","COPY",EDGE,{"derivedFrom":makeQuery(id+"F3.opExtrude","SWEPT_EDGE",EDGE,{"disambiguationData":[OSD([sQuery(id+"F2.wireOp",EDGE,"E21"),sQuery(id+"F2.wireOp",EDGE,"E24")])]})});
            var Q7;
            Q7=makeQuery(id+"F3.boolean.opBoolean","COPY",EDGE,{"derivedFrom":makeQuery(id+"F3.opExtrude","SWEPT_EDGE",EDGE,{"disambiguationData":[OSD([sQuery(id+"F2.wireOp",EDGE,"E24"),sQuery(id+"F2.wireOp",EDGE,"E36.2")])]})});
            var Q8;
            Q8=makeQuery(id+"F3.boolean.opBoolean","COPY",EDGE,{"derivedFrom":makeQuery(id+"F3.opExtrude","SWEPT_EDGE",EDGE,{"disambiguationData":[OSD([sQuery(id+"F2.wireOp",EDGE,"E25"),sQuery(id+"F2.wireOp",EDGE,"E36.5")])]})});
            var Q9;
            Q9=makeQuery(id+"F3.boolean.opBoolean","COPY",EDGE,{"derivedFrom":makeQuery(id+"F3.opExtrude","SWEPT_EDGE",EDGE,{"disambiguationData":[OSD([sQuery(id+"F2.wireOp",EDGE,"E25"),sQuery(id+"F2.wireOp",EDGE,"E31.trimOffspring")])]})});
            var Q10;
            Q10=makeQuery(id+"F3.boolean.opBoolean","COPY",EDGE,{"derivedFrom":makeQuery(id+"F3.opExtrude","SWEPT_EDGE",EDGE,{"disambiguationData":[OSD([sQuery(id+"F2.wireOp",EDGE,"E44"),sQuery(id+"F2.wireOp",EDGE,"E45")])]})});
            var Q11;
            Q11=makeQuery(id+"F3.boolean.opBoolean","COPY",EDGE,{"derivedFrom":makeQuery(id+"F3.opExtrude","SWEPT_EDGE",EDGE,{"disambiguationData":[OSD([sQuery(id+"F2.wireOp",EDGE,"E44"),sQuery(id+"F2.wireOp",EDGE,"E41")])]})});
            var Q12;
            Q12=makeQuery(id+"F3.boolean.opBoolean","COPY",EDGE,{"derivedFrom":makeQuery(id+"F3.opExtrude","SWEPT_EDGE",EDGE,{"disambiguationData":[OSD([sQuery(id+"F0.wireOp",EDGE,"E2"),sQuery(id+"F0.wireOp",EDGE,"E4"),sQuery(id+"F2.wireOp",EDGE,"E18"),sQuery(id+"F2.wireOp",EDGE,"E19")])]})});
            var Q13;
            Q13=makeQuery(id+"F3.boolean.opBoolean","COPY",EDGE,{"derivedFrom":makeQuery(id+"F3.opExtrude","SWEPT_EDGE",EDGE,{"disambiguationData":[OSD([sQuery(id+"F0.wireOp",EDGE,"E5.MirrorCS"),sQuery(id+"F0.wireOp",EDGE,"E6.MirrorCS"),sQuery(id+"F2.wireOp",EDGE,"E16"),sQuery(id+"F2.wireOp",EDGE,"E46")])]})});
            var Q14;
            Q14=makeQuery(id+"F3.boolean.opBoolean","COPY",EDGE,{"derivedFrom":makeQuery(id+"F3.opExtrude","SWEPT_EDGE",EDGE,{"disambiguationData":[OSD([sQuery(id+"F2.wireOp",EDGE,"E15"),sQuery(id+"F2.wireOp",EDGE,"E17")])]})});
            var Q15;
            Q15=makeQuery(id+"F3.boolean.opBoolean","COPY",EDGE,{"derivedFrom":makeQuery(id+"F3.opExtrude","SWEPT_EDGE",EDGE,{"disambiguationData":[OSD([sQuery(id+"F2.wireOp",EDGE,"E21"),sQuery(id+"F2.wireOp",EDGE,"E45")])]})});
            var Q16;
            Q16=makeQuery(id+"F3.boolean.opBoolean","COPY",EDGE,{"derivedFrom":makeQuery(id+"F3.opExtrude","SWEPT_EDGE",EDGE,{"disambiguationData":[OSD([sQuery(id+"F2.wireOp",EDGE,"E47"),sQuery(id+"F2.wireOp",EDGE,"OQKDx2rC-8p01-W7AD-8jVz-H10RrjrdnyRq")])]})});
            var Q17;
            Q17=makeQuery(id+"F3.boolean.opBoolean","COPY",EDGE,{"derivedFrom":makeQuery(id+"F3.opExtrude","SWEPT_EDGE",EDGE,{"disambiguationData":[OSD([sQuery(id+"F2.wireOp",EDGE,"Vc8ZtUI0-CAgl-CdUB-t4W3-tU28hb1vTwv8"),sQuery(id+"F2.wireOp",EDGE,"kiQfGZOA-uULj-dTf1-FmXA-rcEVP8aInjXC")])]})});
            fillet(context, id + "F6", {"entities" : qUnion([Q0, Q1, Q2, Q3, Q4, Q5, Q6, Q7, Q8, Q9, Q10, Q11, Q12, Q13, Q14, Q15, Q16, Q17]), "radius" : 3 * mm, "tangentPropagation" : true, "allowEdgeOverflow" : false});
        }
    });
